# Revit family: Wall family template
name_source: partatom
category: Lighting Fixtures
units: mm (PartAtom-declared; Revit-internal decimal feet)

## family parameters
Always vertical = Yes
Cut with Voids When Loaded = No
Host = Wall
Light Source = No
OmniClass Number = 23.80.70.00
OmniClass Title = Lighting
Part Type = Normal
Room Calculation Point = No
Round Connector Dimension = Use Diameter
Shared = No

## types (2) — shared parameters
Driver Required = No
Manufacturer = Astro Lighting Ltd
Manufacturer URL - Europe and Rest of World = www.astrolighting.com
Manufacturer URL - North America = us.astrolighting.com
URL = www.astrolighting.com
zero-valued in all types: Default Elevation, Electrical Class

## per-type parameters (varying)
| type | ADA compliant | Dimmable | Dimming Method | Driver Included | Efficacy (lm/w) | Lamp | Length of Cable Supplied | Light Source Fixed | Location / IP Rating | Main Material | Power (Watts) | Product CCT | Product CRI | Product Dimensions (MM) | Product Location | Product Name | Product SKU | Product URL | Product Weight (KG) | Wattage Comments |
| CE | N / A | Yes | Lamp Dependent | Not Applicable | Lamp Dependent | E27 | Not Applicable | Yes | Interior / IP20 | Fabric | Lamp Dependent | Lamp Dependent | Lamp Dependent | 130 x 300 x 135 | Wall | Ashino Wide | 1166002 | https://www.astrolighting.com | 0.72 | 12W Max |
| ETL |  |  |  |  |  |  |  |  | DAMP | Metal - Steel |  | 2700K / 3000K | 80 / 90 |  | Bathroom |  | 1234001 |  |  |  |

## geometry (parser evidence)
native form markers: Sweep x3
no freeform markers — native parametric forms only
